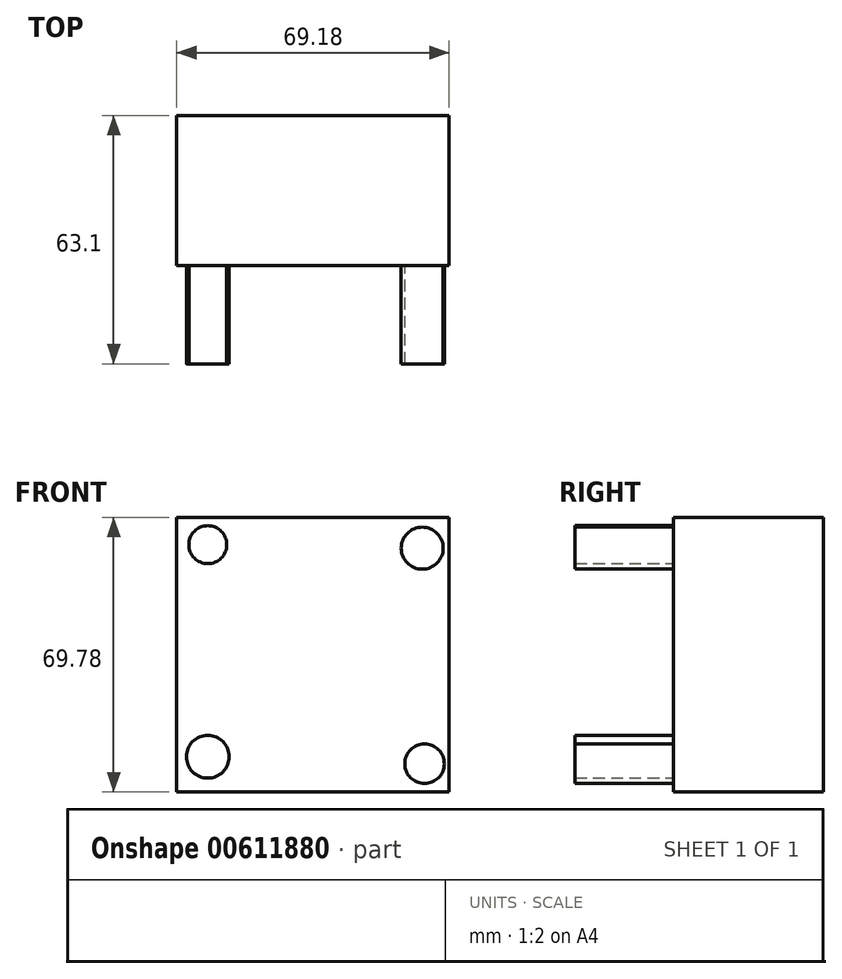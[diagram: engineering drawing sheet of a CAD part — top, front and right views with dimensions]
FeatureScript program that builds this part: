
annotation { "Feature Type Name" : "Feature", "Feature Type Description" : "" }
export const myFeature = defineFeature(function(context is Context, id is Id, definition is map)
    precondition{}
    {
        {
            var Q0;
            Q0=qCreatedBy(makeId("Front.planeOp"),FACE);
            var sketch = newSketch(context, id + "F0", { "sketchPlane" : qUnion([Q0])});
            skLineSegment(sketch, "E0.bottom", {"start": v(-29.93, 45.87) * mm, "end": v(39.25, 45.87) * mm});
            skLineSegment(sketch, "E0.top", {"start": v(-29.93, -23.91) * mm, "end": v(39.25, -23.91) * mm});
            skLineSegment(sketch, "E0.left", {"start": v(-29.93, 45.87) * mm, "end": v(-29.93, -23.91) * mm});
            skLineSegment(sketch, "E0.right", {"start": v(39.25, 45.87) * mm, "end": v(39.25, -23.91) * mm});
            skSolve(sketch);
        }
        {
            var Q0;
            Q0=makeQuery(id+"F0.imprint","IMPRINT",FACE,{"disambiguationData":[TD([[makeQuery(id+"F0.imprint","IMPRINT",EDGE,{"derivedFrom":sQuery(id+"F0.wireOp",EDGE,"E0.bottom")}),-1.0]])]});
            extrude(context, id + "F1", {"entities" : qUnion([Q0]), "depth" : 38.1 * mm, "offsetDistance" : 25.4 * mm});
        }
        {
            var Q0;
            Q0=makeQuery(id+"F1.opExtrude","CAP_FACE",FACE,{"disambiguationData":[OSD([sQuery(id+"F0.wireOp",EDGE,"E0.bottom"),sQuery(id+"F0.wireOp",EDGE,"E0.top"),sQuery(id+"F0.wireOp",EDGE,"E0.left"),sQuery(id+"F0.wireOp",EDGE,"E0.right")])],"isStart":false});
            var sketch = newSketch(context, id + "F2", { "sketchPlane" : qUnion([Q0])});
            skCircle(sketch, "E1", {"center": v(-22.06, 38.93) * mm, "radius": 4.82 * mm});
            skCircle(sketch, "E2", {"center": v(32.42, 38.04) * mm, "radius": 5.34 * mm});
            skCircle(sketch, "E3", {"center": v(33, -16.73) * mm, "radius": 5.02 * mm});
            skCircle(sketch, "E4", {"center": v(-22.06, -14.95) * mm, "radius": 5.43 * mm});
            skSolve(sketch);
        }
        {
            var Q0;
            Q0=makeQuery(id+"F2.imprint","IMPRINT",FACE,{"disambiguationData":[TD([[makeQuery(id+"F2.imprint","IMPRINT",EDGE,{"derivedFrom":sQuery(id+"F2.wireOp",EDGE,"E1")}),1.0]])]});
            var Q1;
            Q1=makeQuery(id+"F2.imprint","IMPRINT",FACE,{"disambiguationData":[TD([[makeQuery(id+"F2.imprint","IMPRINT",EDGE,{"derivedFrom":sQuery(id+"F2.wireOp",EDGE,"E4")}),1.0]])]});
            var Q2;
            Q2=makeQuery(id+"F2.imprint","IMPRINT",FACE,{"disambiguationData":[TD([[makeQuery(id+"F2.imprint","IMPRINT",EDGE,{"derivedFrom":sQuery(id+"F2.wireOp",EDGE,"E3")}),1.0]])]});
            var Q3;
            Q3=makeQuery(id+"F2.imprint","IMPRINT",FACE,{"disambiguationData":[TD([[makeQuery(id+"F2.imprint","IMPRINT",EDGE,{"derivedFrom":sQuery(id+"F2.wireOp",EDGE,"E2")}),1.0]])]});
            extrude(context, id + "F3", {"entities" : qUnion([Q0, Q1, Q2, Q3]), "operationType" : NewBodyOperationType.ADD, "depth" : 25 * mm, "offsetDistance" : 25 * mm});
        }
    });
